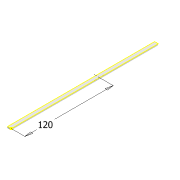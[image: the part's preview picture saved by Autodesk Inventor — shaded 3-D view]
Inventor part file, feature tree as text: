
AUTODESK INVENTOR PART (.ipt)
format: ipt  version: 2022 (Build 260153000, 153)  size: 89,088 bytes
history: native  units: mm
features: sketch x3, extrude x1, projected_geometry x1
ambient origin geometry x8: Origin, YZ Plane, XZ Plane, XY Plane, X Axis, Y Axis, Z Axis, Center Point
bodies: Solid1 (feature_tree)
feature tree (5):
  extrude  "Extrusion1"  Depth=200.0mm
  sketch  "Sketch2"  dims[d2=2.0mm d3=0.0mm]
  sketch  "Sketch3"  dims[d4=120.0mm]
  sketch  "Sketch1"  dims[d0=5.0mm d1=200.0mm]
  projected_geometry  "Projected Loop1"
